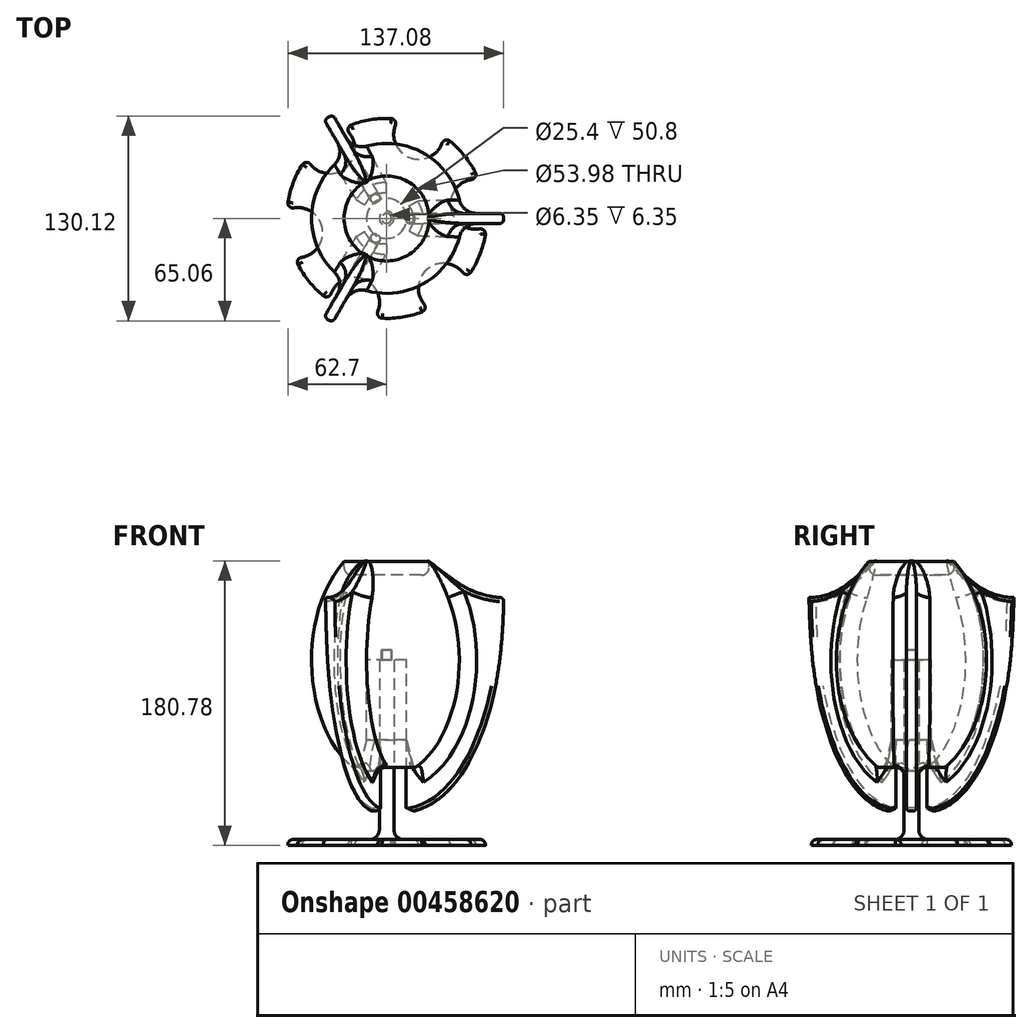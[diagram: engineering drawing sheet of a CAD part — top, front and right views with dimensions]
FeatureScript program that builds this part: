
annotation { "Feature Type Name" : "Feature", "Feature Type Description" : "" }
export const myFeature = defineFeature(function(context is Context, id is Id, definition is map)
    precondition{}
    {
        {
            var Q0;
            Q0=qCreatedBy(makeId("Front.planeOp"),FACE);
            var sketch = newSketch(context, id + "F0", { "sketchPlane" : qUnion([Q0])});
            skEllipticalArc(sketch, "E0", {});
            skLineSegment(sketch, "E1", {"start": v(0, 53.97) * mm, "end": v(0, 6.35) * mm});
            skLineSegment(sketch, "E2", {"start": v(3.18, 0) * mm, "end": v(47.63, 0) * mm});
            skLineSegment(sketch, "E3", {"start": v(12.7, -50.8) * mm, "end": v(35.5, -50.8) * mm});
            skLineSegment(sketch, "E4", {"start": v(0, 53.97) * mm, "end": v(33.62, 53.97) * mm});
            skLineSegment(sketch, "E5", {"start": v(26.99, 53.97) * mm, "end": v(26.99, 62.78) * mm});
            skLineSegment(sketch, "E6", {"start": v(12.7, 0) * mm, "end": v(12.7, -50.8) * mm});
            skLineSegment(sketch, "E7", {"start": v(12.7, -50.8) * mm, "end": v(17.75, -70.71) * mm});
            skPoint(sketch, "E7.endSnap0", {"position": v(17.75, -50.8) * mm});
            skLineSegment(sketch, "E8", {"start": v(3.18, 0) * mm, "end": v(3.17, 6.35) * mm});
            skLineSegment(sketch, "E9", {"start": v(3.17, 6.35) * mm, "end": v(0, 6.35) * mm});
            skPoint(sketch, "E10.orphan", {"position": v(0, -50.8) * mm});
            const initialGuessF0  = {"E0": [0, 0, 0, -1, 0.0762, 0.047625, 0.38189324819891574, 2.539138020204803]};
            skSetInitialGuess(sketch, initialGuessF0);
            skSolve(sketch);
        }
        {
            var Q0;
            Q0=qCreatedBy(makeId("Front.planeOp"),FACE);
            var sketch = newSketch(context, id + "F1", { "sketchPlane" : qUnion([Q0])});
            skSolve(sketch);
        }
        {
            var Q0;
            Q0 = qSketchRegion(id + "F1", true);
            var Q1;
            {var subQ5=sQuery(id+"F0.wireOp",EDGE,"E1");Q1=makeQuery(id+"F0.imprint","IMPRINT",FACE,{"disambiguationData":[TD([[makeQuery(id+"F0.imprint","IMPRINT",EDGE,{"derivedFrom":subQ5}),1.0]])]});}
            var Q2;
            {var subQ3=sQuery(id+"F0.wireOp",EDGE,"E3");Q2=makeQuery(id+"F0.imprint","IMPRINT",FACE,{"disambiguationData":[TD([[makeQuery(id+"F0.imprint","IMPRINT",EDGE,{"derivedFrom":subQ3}),1.0]])]});}
            var Q3;
            {var subQ2=sQuery(id+"F0.wireOp",EDGE,"E3");Q3=makeQuery(id+"F0.imprint","IMPRINT",FACE,{"disambiguationData":[TD([[makeQuery(id+"F0.imprint","IMPRINT",EDGE,{"derivedFrom":subQ2}),-1.0]])]});}
            var Q4;
            {var subQ0=sQuery(id+"F0.wireOp",EDGE,"E5");Q4=makeQuery(id+"F0.imprint","IMPRINT",FACE,{"disambiguationData":[TD([[makeQuery(id+"F0.imprint","IMPRINT",EDGE,{"derivedFrom":subQ0}),-1.0]])]});}
            var Q5;
            Q5=sQuery(id+"F0.wireOp",EDGE,"E1");
            revolve(context, id + "F2", {"entities" : qUnion([Q0, Q1, Q2, Q3, Q4]), "axis" : qUnion([Q5]), "revolveType" : RevolveType.FULL});
        }
        {
            var Q0;
            Q0=qCreatedBy(makeId("Front.planeOp"),FACE);
            var sketch = newSketch(context, id + "F3", { "sketchPlane" : qUnion([Q0])});
            skEllipticalArc(sketch, "E11.0", {});
            skFitSpline(sketch, "E12", {"points": [v(17.75, -96.11) * mm, v(62.2, -43.9) * mm, v(74.95, 39.51) * mm], "startDerivative": vector(138.34, 33.42) * mm, "endDerivative": vector(4.15, 174.83) * mm});
            skFitSpline(sketch, "E13", {"points": [v(26.99, 62.78) * mm, v(52.93, 44.73) * mm, v(74.95, 39.51) * mm], "startDerivative": vector(53.6, -38.1) * mm, "endDerivative": vector(42.04, 0.55) * mm});
            skArc(sketch, "E14", {"start": v(73.77, 14.42) * mm, "mid": v(56.44, 0.7) * mm, "end": v(69.62, -17.04) * mm});
            skFitSpline(sketch, "E15.trimOffspring", {"points": [v(17.75, -96.11) * mm, v(62.2, -43.9) * mm, v(74.95, 39.51) * mm], "startDerivative": vector(138.34, 33.42) * mm, "endDerivative": vector(4.15, 174.83) * mm});
            skEllipticalArc(sketch, "E16.0.2", {});
            skLineSegment(sketch, "E16.0.5", {"start": v(0, 53.97) * mm, "end": v(0, 6.35) * mm});
            skPoint(sketch, "E16.0.0.end.orphan", {"position": v(12.7, 0) * mm});
            skPoint(sketch, "E16.0.3.end.orphan", {"position": v(26.99, 53.97) * mm});
            skPoint(sketch, "E16.0.7.end.orphan", {"position": v(3.18, 0) * mm});
            skPoint(sketch, "E16.0.6.end.orphan", {"position": v(3.17, 6.35) * mm});
            skLineSegment(sketch, "E17.0", {"start": v(12.7, -50.8) * mm, "end": v(17.75, -70.71) * mm});
            skLineSegment(sketch, "E18", {"start": v(17.75, -70.71) * mm, "end": v(12.7, -50.8) * mm});
            skLineSegment(sketch, "E19", {"start": v(12.7, -50.8) * mm, "end": v(12.7, -93.82) * mm});
            skLineSegment(sketch, "E20", {"start": v(17.75, -96.11) * mm, "end": v(12.7, -93.82) * mm});
            const initialGuessF3  = {"E11.0": [0, 0, 0, -1, 0.0762, 0.047625, 0.38189324819891574, 2.579056409045938], "E16.0.2": [0, 0, 0, -1, 0.0762, 0.047625, 1.5707963267948966, 2.300523983021863]};
            skSetInitialGuess(sketch, initialGuessF3);
            skSolve(sketch);
        }
        {
            var Q0;
            Q0 = qSketchRegion(id + "F3", true);
            extrude(context, id + "F4", {"entities" : qUnion([Q0]), "endBound" : BoundingType.SYMMETRIC, "depth" : 6.35 * mm});
        }
        {
            var Q0;
            Q0=makeQuery(id+"F4.opExtrude","SWEPT_BODY",BODY,{"disambiguationData":[OSD([sQuery(id+"F3.wireOp",EDGE,"E11.0"),sQuery(id+"F3.wireOp",EDGE,"7cff1985-20f7-4c6d-82bb-5eb624a96f58"),sQuery(id+"F3.wireOp",EDGE,"E12"),sQuery(id+"F3.wireOp",EDGE,"E13"),sQuery(id+"F3.wireOp",EDGE,"E14"),sQuery(id+"F3.wireOp",EDGE,"E15.trimOffspring"),sQuery(id+"F3.wireOp",EDGE,"E16.0.2")])]});
            var Q1;
            Q1=sQuery(id+"F3.wireOp",EDGE,"E16.0.5");
            circularPattern(context, id + "F5", {"entities" : qUnion([Q0]), "axis" : qUnion([Q1]), "angle" : 360 * degree, "instanceCount" : 3, "equalSpace" : true});
        }
        {
            var Q0;
            Q0=qCreatedBy(makeId("Front.planeOp"),FACE);
            var sketch = newSketch(context, id + "F6", { "sketchPlane" : qUnion([Q0])});
            skPoint(sketch, "E21.0", {"position": v(0, 6.35) * mm});
            skLineSegment(sketch, "E22", {"start": v(0, 6.35) * mm, "end": v(3.05, 6.35) * mm});
            skLineSegment(sketch, "E23", {"start": v(3.05, 6.35) * mm, "end": v(3.05, 0) * mm});
            skLineSegment(sketch, "E24", {"start": v(3.05, 0) * mm, "end": v(4.64, 0) * mm});
            skLineSegment(sketch, "E25", {"start": v(4.64, 0) * mm, "end": v(4.64, -107.58) * mm});
            skLineSegment(sketch, "E26", {"start": v(10.99, -113.93) * mm, "end": v(60.33, -113.93) * mm});
            skLineSegment(sketch, "E27", {"start": v(63.5, -117.1) * mm, "end": v(63.5, -117.74) * mm});
            skLineSegment(sketch, "E28", {"start": v(63.5, -117.74) * mm, "end": v(0, -117.74) * mm});
            skLineSegment(sketch, "E29", {"start": v(0, -117.74) * mm, "end": v(0, 6.35) * mm});
            skPoint(sketch, "E30.visualSharp", {"position": v(4.64, -113.93) * mm});
            skArc(sketch, "E30.filletArc", {"start": v(4.64, -107.58) * mm, "mid": v(6.5, -112.07) * mm, "end": v(10.99, -113.93) * mm});
            skPoint(sketch, "E31.visualSharp", {"position": v(63.5, -113.93) * mm});
            skArc(sketch, "E31.filletArc", {"start": v(63.5, -117.1) * mm, "mid": v(62.57, -114.86) * mm, "end": v(60.33, -113.93) * mm});
            skSolve(sketch);
        }
        {
            var Q0;
            Q0=makeQuery(id+"F6.imprint","IMPRINT",FACE,{"disambiguationData":[TD([[makeQuery(id+"F6.imprint","IMPRINT",EDGE,{"derivedFrom":sQuery(id+"F6.wireOp",EDGE,"E22")}),-1.0]])]});
            var Q1;
            Q1=sQuery(id+"F6.wireOp",EDGE,"E29");
            revolve(context, id + "F7", {"entities" : qUnion([Q0]), "axis" : qUnion([Q1]), "revolveType" : RevolveType.FULL});
        }
        {
            var Q0;
            Q0=makeQuery(id+"F4.opExtrude","CAP_EDGE",EDGE,{"disambiguationData":[OSD([sQuery(id+"F3.wireOp",EDGE,"E13")])],"isStart":false});
            fillet(context, id + "F8", {"entities" : qUnion([Q0]), "radius" : 2.54 * mm, "tangentPropagation" : true, "allowEdgeOverflow" : false});
        }
        {
            var Q0;
            Q0=makeQuery(id+"F4.opExtrude","CAP_EDGE",EDGE,{"disambiguationData":[OSD([sQuery(id+"F3.wireOp",EDGE,"E13")])],"isStart":true});
            var Q1;
            Q1=makeQuery(id+"F4.opExtrude","CAP_EDGE",EDGE,{"disambiguationData":[OSD([sQuery(id+"F3.wireOp",EDGE,"E15.trimOffspring")])],"isStart":false});
            var Q2;
            Q2=makeQuery(id+"F4.opExtrude","CAP_EDGE",EDGE,{"disambiguationData":[OSD([sQuery(id+"F3.wireOp",EDGE,"E15.trimOffspring")])],"isStart":true});
            var Q3;
            Q3=makeQuery(id+"F4.opExtrude","CAP_EDGE",EDGE,{"disambiguationData":[OSD([sQuery(id+"F3.wireOp",EDGE,"E12")])],"isStart":false});
            var Q4;
            Q4=makeQuery(id+"F4.opExtrude","CAP_EDGE",EDGE,{"disambiguationData":[OSD([sQuery(id+"F3.wireOp",EDGE,"E12")])],"isStart":true});
            var Q5;
            Q5=makeQuery(id+"F4.opExtrude","CAP_EDGE",EDGE,{"disambiguationData":[OSD([sQuery(id+"F3.wireOp",EDGE,"E14")])],"isStart":false});
            var Q6;
            Q6=makeQuery(id+"F4.opExtrude","CAP_EDGE",EDGE,{"disambiguationData":[OSD([sQuery(id+"F3.wireOp",EDGE,"E14")])],"isStart":true});
            fillet(context, id + "F9", {"entities" : qUnion([Q0, Q1, Q2, Q3, Q4, Q5, Q6]), "radius" : 2.54 * mm, "tangentPropagation" : true, "allowEdgeOverflow" : false});
        }
        {
            var Q0;
            Q0=makeQuery(id+"F5.opPattern","COPY",EDGE,{"derivedFrom":makeQuery(id+"F4.opExtrude","CAP_EDGE",EDGE,{"disambiguationData":[OSD([sQuery(id+"F3.wireOp",EDGE,"E15.trimOffspring")])],"isStart":false}),"instanceName":"1"});
            var Q1;
            Q1=makeQuery(id+"F5.opPattern","COPY",EDGE,{"derivedFrom":makeQuery(id+"F4.opExtrude","CAP_EDGE",EDGE,{"disambiguationData":[OSD([sQuery(id+"F3.wireOp",EDGE,"E15.trimOffspring")])],"isStart":true}),"instanceName":"1"});
            var Q2;
            Q2=makeQuery(id+"F5.opPattern","COPY",EDGE,{"derivedFrom":makeQuery(id+"F4.opExtrude","CAP_EDGE",EDGE,{"disambiguationData":[OSD([sQuery(id+"F3.wireOp",EDGE,"E14")])],"isStart":false}),"instanceName":"1"});
            var Q3;
            Q3=makeQuery(id+"F5.opPattern","COPY",EDGE,{"derivedFrom":makeQuery(id+"F4.opExtrude","CAP_EDGE",EDGE,{"disambiguationData":[OSD([sQuery(id+"F3.wireOp",EDGE,"E14")])],"isStart":true}),"instanceName":"1"});
            var Q4;
            Q4=makeQuery(id+"F5.opPattern","COPY",EDGE,{"derivedFrom":makeQuery(id+"F4.opExtrude","CAP_EDGE",EDGE,{"disambiguationData":[OSD([sQuery(id+"F3.wireOp",EDGE,"E12")])],"isStart":true}),"instanceName":"1"});
            var Q5;
            Q5=makeQuery(id+"F5.opPattern","COPY",EDGE,{"derivedFrom":makeQuery(id+"F4.opExtrude","CAP_EDGE",EDGE,{"disambiguationData":[OSD([sQuery(id+"F3.wireOp",EDGE,"E12")])],"isStart":false}),"instanceName":"1"});
            var Q6;
            Q6=makeQuery(id+"F5.opPattern","COPY",EDGE,{"derivedFrom":makeQuery(id+"F4.opExtrude","CAP_EDGE",EDGE,{"disambiguationData":[OSD([sQuery(id+"F3.wireOp",EDGE,"E13")])],"isStart":false}),"instanceName":"1"});
            var Q7;
            Q7=makeQuery(id+"F5.opPattern","COPY",EDGE,{"derivedFrom":makeQuery(id+"F4.opExtrude","CAP_EDGE",EDGE,{"disambiguationData":[OSD([sQuery(id+"F3.wireOp",EDGE,"E13")])],"isStart":true}),"instanceName":"1"});
            fillet(context, id + "F10", {"entities" : qUnion([Q0, Q1, Q2, Q3, Q4, Q5, Q6, Q7]), "radius" : 2.54 * mm, "tangentPropagation" : true, "allowEdgeOverflow" : false});
        }
        {
            var Q0;
            Q0=makeQuery(id+"F5.opPattern","COPY",EDGE,{"derivedFrom":makeQuery(id+"F4.opExtrude","CAP_EDGE",EDGE,{"disambiguationData":[OSD([sQuery(id+"F3.wireOp",EDGE,"E12")])],"isStart":true}),"instanceName":"2"});
            var Q1;
            Q1=makeQuery(id+"F5.opPattern","COPY",EDGE,{"derivedFrom":makeQuery(id+"F4.opExtrude","CAP_EDGE",EDGE,{"disambiguationData":[OSD([sQuery(id+"F3.wireOp",EDGE,"E14")])],"isStart":false}),"instanceName":"2"});
            var Q2;
            Q2=makeQuery(id+"F5.opPattern","COPY",EDGE,{"derivedFrom":makeQuery(id+"F4.opExtrude","CAP_EDGE",EDGE,{"disambiguationData":[OSD([sQuery(id+"F3.wireOp",EDGE,"E14")])],"isStart":true}),"instanceName":"2"});
            var Q3;
            Q3=makeQuery(id+"F5.opPattern","COPY",EDGE,{"derivedFrom":makeQuery(id+"F4.opExtrude","CAP_EDGE",EDGE,{"disambiguationData":[OSD([sQuery(id+"F3.wireOp",EDGE,"E15.trimOffspring")])],"isStart":false}),"instanceName":"2"});
            var Q4;
            Q4=makeQuery(id+"F5.opPattern","COPY",EDGE,{"derivedFrom":makeQuery(id+"F4.opExtrude","CAP_EDGE",EDGE,{"disambiguationData":[OSD([sQuery(id+"F3.wireOp",EDGE,"E15.trimOffspring")])],"isStart":true}),"instanceName":"2"});
            var Q5;
            Q5=makeQuery(id+"F5.opPattern","COPY",EDGE,{"derivedFrom":makeQuery(id+"F4.opExtrude","CAP_EDGE",EDGE,{"disambiguationData":[OSD([sQuery(id+"F3.wireOp",EDGE,"E13")])],"isStart":false}),"instanceName":"2"});
            var Q6;
            Q6=makeQuery(id+"F5.opPattern","COPY",EDGE,{"derivedFrom":makeQuery(id+"F4.opExtrude","CAP_EDGE",EDGE,{"disambiguationData":[OSD([sQuery(id+"F3.wireOp",EDGE,"E13")])],"isStart":true}),"instanceName":"2"});
            var Q7;
            Q7=makeQuery(id+"F5.opPattern","COPY",EDGE,{"derivedFrom":makeQuery(id+"F4.opExtrude","CAP_EDGE",EDGE,{"disambiguationData":[OSD([sQuery(id+"F3.wireOp",EDGE,"E12")])],"isStart":false}),"instanceName":"2"});
            fillet(context, id + "F11", {"entities" : qUnion([Q0, Q1, Q2, Q3, Q4, Q5, Q6, Q7]), "radius" : 2.54 * mm, "tangentPropagation" : true, "allowEdgeOverflow" : false});
        }
        {
            var Q0;
            Q0=makeQuery(id+"F5.opPattern","COPY",EDGE,{"derivedFrom":makeQuery(id+"F4.opExtrude","CAP_EDGE",EDGE,{"disambiguationData":[OSD([sQuery(id+"F3.wireOp",EDGE,"E19")])],"isStart":false}),"instanceName":"1"});
            var Q1;
            Q1=makeQuery(id+"F5.opPattern","COPY",EDGE,{"derivedFrom":makeQuery(id+"F4.opExtrude","CAP_EDGE",EDGE,{"disambiguationData":[OSD([sQuery(id+"F3.wireOp",EDGE,"E19")])],"isStart":true}),"instanceName":"1"});
            var Q2;
            Q2=makeQuery(id+"F10.opFillet","BLEND_EDGE",EDGE,{"blendedFrom":[makeQuery(id+"F5.opPattern","COPY",EDGE,{"derivedFrom":makeQuery(id+"F4.opExtrude","CAP_EDGE",EDGE,{"disambiguationData":[OSD([sQuery(id+"F3.wireOp",EDGE,"E12")])],"isStart":false}),"instanceName":"1"}),makeQuery(id+"F5.opPattern","COPY",FACE,{"derivedFrom":makeQuery(id+"F4.opExtrude","SWEPT_FACE",FACE,{"disambiguationData":[OSD([sQuery(id+"F3.wireOp",EDGE,"E20")])]}),"instanceName":"1"})],"blendedInto":[makeQuery(id+"F5.opPattern","COPY",FACE,{"derivedFrom":makeQuery(id+"F4.opExtrude","SWEPT_FACE",FACE,{"disambiguationData":[OSD([sQuery(id+"F3.wireOp",EDGE,"E20")])]}),"instanceName":"1"})]});
            var Q3;
            Q3=makeQuery(id+"F10.opFillet","BLEND_EDGE",EDGE,{"blendedFrom":[makeQuery(id+"F5.opPattern","COPY",EDGE,{"derivedFrom":makeQuery(id+"F4.opExtrude","CAP_EDGE",EDGE,{"disambiguationData":[OSD([sQuery(id+"F3.wireOp",EDGE,"E12")])],"isStart":true}),"instanceName":"1"}),makeQuery(id+"F5.opPattern","COPY",FACE,{"derivedFrom":makeQuery(id+"F4.opExtrude","SWEPT_FACE",FACE,{"disambiguationData":[OSD([sQuery(id+"F3.wireOp",EDGE,"E20")])]}),"instanceName":"1"})],"blendedInto":[makeQuery(id+"F5.opPattern","COPY",FACE,{"derivedFrom":makeQuery(id+"F4.opExtrude","SWEPT_FACE",FACE,{"disambiguationData":[OSD([sQuery(id+"F3.wireOp",EDGE,"E20")])]}),"instanceName":"1"})]});
            var Q4;
            Q4=makeQuery(id+"F4.opExtrude","CAP_EDGE",EDGE,{"disambiguationData":[OSD([sQuery(id+"F3.wireOp",EDGE,"E19")])],"isStart":false});
            var Q5;
            Q5=makeQuery(id+"F4.opExtrude","CAP_EDGE",EDGE,{"disambiguationData":[OSD([sQuery(id+"F3.wireOp",EDGE,"E19")])],"isStart":true});
            var Q6;
            Q6=makeQuery(id+"F9.opFillet","BLEND_EDGE",EDGE,{"blendedFrom":[makeQuery(id+"F4.opExtrude","CAP_EDGE",EDGE,{"disambiguationData":[OSD([sQuery(id+"F3.wireOp",EDGE,"E12")])],"isStart":false}),makeQuery(id+"F4.opExtrude","SWEPT_FACE",FACE,{"disambiguationData":[OSD([sQuery(id+"F3.wireOp",EDGE,"E20")])]})],"blendedInto":[makeQuery(id+"F4.opExtrude","SWEPT_FACE",FACE,{"disambiguationData":[OSD([sQuery(id+"F3.wireOp",EDGE,"E20")])]})]});
            var Q7;
            Q7=makeQuery(id+"F5.opPattern","COPY",EDGE,{"derivedFrom":makeQuery(id+"F4.opExtrude","CAP_EDGE",EDGE,{"disambiguationData":[OSD([sQuery(id+"F3.wireOp",EDGE,"E19")])],"isStart":true}),"instanceName":"2"});
            var Q8;
            Q8=makeQuery(id+"F5.opPattern","COPY",EDGE,{"derivedFrom":makeQuery(id+"F4.opExtrude","CAP_EDGE",EDGE,{"disambiguationData":[OSD([sQuery(id+"F3.wireOp",EDGE,"E19")])],"isStart":false}),"instanceName":"2"});
            var Q9;
            Q9=makeQuery(id+"F11.opFillet","BLEND_EDGE",EDGE,{"blendedFrom":[makeQuery(id+"F5.opPattern","COPY",EDGE,{"derivedFrom":makeQuery(id+"F4.opExtrude","CAP_EDGE",EDGE,{"disambiguationData":[OSD([sQuery(id+"F3.wireOp",EDGE,"E12")])],"isStart":true}),"instanceName":"2"}),makeQuery(id+"F5.opPattern","COPY",FACE,{"derivedFrom":makeQuery(id+"F4.opExtrude","SWEPT_FACE",FACE,{"disambiguationData":[OSD([sQuery(id+"F3.wireOp",EDGE,"E20")])]}),"instanceName":"2"})],"blendedInto":[makeQuery(id+"F5.opPattern","COPY",FACE,{"derivedFrom":makeQuery(id+"F4.opExtrude","SWEPT_FACE",FACE,{"disambiguationData":[OSD([sQuery(id+"F3.wireOp",EDGE,"E20")])]}),"instanceName":"2"})]});
            fillet(context, id + "F12", {"entities" : qUnion([Q0, Q1, Q2, Q3, Q4, Q5, Q6, Q7, Q8, Q9]), "radius" : 2.54 * mm, "tangentPropagation" : true, "allowEdgeOverflow" : false});
        }
        {
            var Q0;
            Q0=makeQuery(id+"F2.opRevolve","SWEPT_EDGE",EDGE,{"disambiguationData":[OSD([sQuery(id+"F0.wireOp",EDGE,"E4"),sQuery(id+"F0.wireOp",EDGE,"E5")])]});
            fillet(context, id + "F13", {"entities" : qUnion([Q0]), "radius" : 5.08 * mm, "tangentPropagation" : true, "allowEdgeOverflow" : false});
        }
        {
            var Q0;
            Q0=makeQuery(id+"F5.opPattern","COPY",BODY,{"derivedFrom":makeQuery(id+"F4.opExtrude","SWEPT_BODY",BODY,{"disambiguationData":[OSD([sQuery(id+"F3.wireOp",EDGE,"E11.0"),sQuery(id+"F3.wireOp",EDGE,"E12"),sQuery(id+"F3.wireOp",EDGE,"E13"),sQuery(id+"F3.wireOp",EDGE,"E14"),sQuery(id+"F3.wireOp",EDGE,"E15.trimOffspring"),sQuery(id+"F3.wireOp",EDGE,"E16.0.2"),sQuery(id+"F3.wireOp",EDGE,"E18"),sQuery(id+"F3.wireOp",EDGE,"E19"),sQuery(id+"F3.wireOp",EDGE,"E20")])]}),"instanceName":"2"});
            transform(context, id + "F14", {"entities" : qUnion([Q0]), "transformType" : TransformType.TRANSLATION_3D, "dx" : 0.5 * mm, "dy" : -0.5 * mm, "dz" : 0.25 * mm, "makeCopy" : false});
        }
        {
            var Q0;
            Q0=makeQuery(id+"F5.opPattern","COPY",BODY,{"derivedFrom":makeQuery(id+"F4.opExtrude","SWEPT_BODY",BODY,{"disambiguationData":[OSD([sQuery(id+"F3.wireOp",EDGE,"E11.0"),sQuery(id+"F3.wireOp",EDGE,"E12"),sQuery(id+"F3.wireOp",EDGE,"E13"),sQuery(id+"F3.wireOp",EDGE,"E14"),sQuery(id+"F3.wireOp",EDGE,"E15.trimOffspring"),sQuery(id+"F3.wireOp",EDGE,"E16.0.2"),sQuery(id+"F3.wireOp",EDGE,"E18"),sQuery(id+"F3.wireOp",EDGE,"E19"),sQuery(id+"F3.wireOp",EDGE,"E20")])]}),"instanceName":"1"});
            transform(context, id + "F15", {"entities" : qUnion([Q0]), "transformType" : TransformType.TRANSLATION_3D, "dx" : 0.5 * mm, "dy" : 0.5 * mm, "dz" : 0.25 * mm, "makeCopy" : false});
        }
        {
            var Q0;
            Q0=makeQuery(id+"F4.opExtrude","SWEPT_BODY",BODY,{"disambiguationData":[OSD([sQuery(id+"F3.wireOp",EDGE,"E11.0"),sQuery(id+"F3.wireOp",EDGE,"E12"),sQuery(id+"F3.wireOp",EDGE,"E13"),sQuery(id+"F3.wireOp",EDGE,"E14"),sQuery(id+"F3.wireOp",EDGE,"E15.trimOffspring"),sQuery(id+"F3.wireOp",EDGE,"E16.0.2"),sQuery(id+"F3.wireOp",EDGE,"E18"),sQuery(id+"F3.wireOp",EDGE,"E19"),sQuery(id+"F3.wireOp",EDGE,"E20")])]});
            transform(context, id + "F16", {"entities" : qUnion([Q0]), "transformType" : TransformType.TRANSLATION_3D, "dx" : -0.5 * mm, "dy" : 0 * mm, "dz" : 0.25 * mm, "makeCopy" : false});
        }
        {
            var Q0;
            Q0=makeQuery(id+"F2.opRevolve","SWEPT_BODY",BODY,{"disambiguationData":[OSD([sQuery(id+"F0.wireOp",EDGE,"E0"),sQuery(id+"F0.wireOp",EDGE,"E1"),sQuery(id+"F0.wireOp",EDGE,"E2"),sQuery(id+"F0.wireOp",EDGE,"E4"),sQuery(id+"F0.wireOp",EDGE,"E5"),sQuery(id+"F0.wireOp",EDGE,"E6"),sQuery(id+"F0.wireOp",EDGE,"E7"),sQuery(id+"F0.wireOp",EDGE,"E8"),sQuery(id+"F0.wireOp",EDGE,"E9")])]});
            var Q1;
            Q1=makeQuery(id+"F4.opExtrude","SWEPT_BODY",BODY,{"disambiguationData":[OSD([sQuery(id+"F3.wireOp",EDGE,"E11.0"),sQuery(id+"F3.wireOp",EDGE,"E12"),sQuery(id+"F3.wireOp",EDGE,"E13"),sQuery(id+"F3.wireOp",EDGE,"E14"),sQuery(id+"F3.wireOp",EDGE,"E15.trimOffspring"),sQuery(id+"F3.wireOp",EDGE,"E16.0.2"),sQuery(id+"F3.wireOp",EDGE,"E18"),sQuery(id+"F3.wireOp",EDGE,"E19"),sQuery(id+"F3.wireOp",EDGE,"E20")])]});
            var Q2;
            Q2=makeQuery(id+"F5.opPattern","COPY",BODY,{"derivedFrom":makeQuery(id+"F4.opExtrude","SWEPT_BODY",BODY,{"disambiguationData":[OSD([sQuery(id+"F3.wireOp",EDGE,"E11.0"),sQuery(id+"F3.wireOp",EDGE,"E12"),sQuery(id+"F3.wireOp",EDGE,"E13"),sQuery(id+"F3.wireOp",EDGE,"E14"),sQuery(id+"F3.wireOp",EDGE,"E15.trimOffspring"),sQuery(id+"F3.wireOp",EDGE,"E16.0.2"),sQuery(id+"F3.wireOp",EDGE,"E18"),sQuery(id+"F3.wireOp",EDGE,"E19"),sQuery(id+"F3.wireOp",EDGE,"E20")])]}),"instanceName":"1"});
            var Q3;
            Q3=makeQuery(id+"F5.opPattern","COPY",BODY,{"derivedFrom":makeQuery(id+"F4.opExtrude","SWEPT_BODY",BODY,{"disambiguationData":[OSD([sQuery(id+"F3.wireOp",EDGE,"E11.0"),sQuery(id+"F3.wireOp",EDGE,"E12"),sQuery(id+"F3.wireOp",EDGE,"E13"),sQuery(id+"F3.wireOp",EDGE,"E14"),sQuery(id+"F3.wireOp",EDGE,"E15.trimOffspring"),sQuery(id+"F3.wireOp",EDGE,"E16.0.2"),sQuery(id+"F3.wireOp",EDGE,"E18"),sQuery(id+"F3.wireOp",EDGE,"E19"),sQuery(id+"F3.wireOp",EDGE,"E20")])]}),"instanceName":"2"});
            booleanBodies(context, id + "F17", {"operationType" : BooleanOperationType.UNION, "tools" : qUnion([Q0, Q1, Q2, Q3])});
        }
        {
            var Q0;
            Q0=makeQuery(id+"F17.opBoolean","INTERSECT",EDGE,{"derivedFrom":[makeQuery(id+"F2.opRevolve","SWEPT_FACE",FACE,{"disambiguationData":[OSD([sQuery(id+"F0.wireOp",EDGE,"E0")])]}),makeQuery(id+"F4.opExtrude","CAP_FACE",FACE,{"disambiguationData":[OSD([sQuery(id+"F3.wireOp",EDGE,"E11.0"),sQuery(id+"F3.wireOp",EDGE,"E12"),sQuery(id+"F3.wireOp",EDGE,"E13"),sQuery(id+"F3.wireOp",EDGE,"E14"),sQuery(id+"F3.wireOp",EDGE,"E15.trimOffspring"),sQuery(id+"F3.wireOp",EDGE,"E16.0.2"),sQuery(id+"F3.wireOp",EDGE,"E18"),sQuery(id+"F3.wireOp",EDGE,"E19"),sQuery(id+"F3.wireOp",EDGE,"E20")])],"isStart":false})]});
            var Q1;
            Q1=makeQuery(id+"F17.opBoolean","INTERSECT",EDGE,{"derivedFrom":[makeQuery(id+"F2.opRevolve","SWEPT_FACE",FACE,{"disambiguationData":[OSD([sQuery(id+"F0.wireOp",EDGE,"E0")])]}),makeQuery(id+"F5.opPattern","COPY",FACE,{"derivedFrom":makeQuery(id+"F4.opExtrude","CAP_FACE",FACE,{"disambiguationData":[OSD([sQuery(id+"F3.wireOp",EDGE,"E11.0"),sQuery(id+"F3.wireOp",EDGE,"E12"),sQuery(id+"F3.wireOp",EDGE,"E13"),sQuery(id+"F3.wireOp",EDGE,"E14"),sQuery(id+"F3.wireOp",EDGE,"E15.trimOffspring"),sQuery(id+"F3.wireOp",EDGE,"E16.0.2"),sQuery(id+"F3.wireOp",EDGE,"E18"),sQuery(id+"F3.wireOp",EDGE,"E19"),sQuery(id+"F3.wireOp",EDGE,"E20")])],"isStart":true}),"instanceName":"1"})]});
            var Q2;
            Q2=makeQuery(id+"F17.opBoolean","INTERSECT",EDGE,{"derivedFrom":[makeQuery(id+"F2.opRevolve","SWEPT_FACE",FACE,{"disambiguationData":[OSD([sQuery(id+"F0.wireOp",EDGE,"E0")])]}),makeQuery(id+"F5.opPattern","COPY",FACE,{"derivedFrom":makeQuery(id+"F4.opExtrude","CAP_FACE",FACE,{"disambiguationData":[OSD([sQuery(id+"F3.wireOp",EDGE,"E11.0"),sQuery(id+"F3.wireOp",EDGE,"E12"),sQuery(id+"F3.wireOp",EDGE,"E13"),sQuery(id+"F3.wireOp",EDGE,"E14"),sQuery(id+"F3.wireOp",EDGE,"E15.trimOffspring"),sQuery(id+"F3.wireOp",EDGE,"E16.0.2"),sQuery(id+"F3.wireOp",EDGE,"E18"),sQuery(id+"F3.wireOp",EDGE,"E19"),sQuery(id+"F3.wireOp",EDGE,"E20")])],"isStart":true}),"instanceName":"2"})]});
            fillet(context, id + "F18", {"entities" : qUnion([Q0, Q1, Q2]), "radius" : 11.43 * mm, "tangentPropagation" : true, "allowEdgeOverflow" : false});
        }
        {
            var Q0;
            {var subQ0=sQuery(id+"F0.wireOp",EDGE,"E0");var subQ1=sQuery(id+"F0.wireOp",EDGE,"E7");var subQ2=sQuery(id+"F3.wireOp",EDGE,"E20");var subQ3=sQuery(id+"F3.wireOp",EDGE,"E19");var subQ4=sQuery(id+"F3.wireOp",EDGE,"E18");var subQ5=sQuery(id+"F3.wireOp",EDGE,"E16.0.2");var subQ6=sQuery(id+"F3.wireOp",EDGE,"E15.trimOffspring");var subQ7=sQuery(id+"F3.wireOp",EDGE,"E14");var subQ8=sQuery(id+"F3.wireOp",EDGE,"E13");var subQ9=sQuery(id+"F3.wireOp",EDGE,"E12");var subQ10=sQuery(id+"F3.wireOp",EDGE,"E11.0");Q0=makeQuery(id+"F17.opBoolean","SPLIT",EDGE,{"disambiguationData":[TD([makeQuery(id+"F4.opExtrude","CAP_FACE",FACE,{"disambiguationData":[OSD([subQ10,subQ9,subQ8,subQ7,subQ6,subQ5,subQ4,subQ3,subQ2])],"isStart":true})])],"derivedFrom":makeQuery(id+"F2.opRevolve","SWEPT_EDGE",EDGE,{"disambiguationData":[OSD([subQ0,subQ1])]})});}
            var Q1;
            {var subQ0=sQuery(id+"F0.wireOp",EDGE,"E0");var subQ1=sQuery(id+"F0.wireOp",EDGE,"E7");var subQ2=sQuery(id+"F3.wireOp",EDGE,"E20");var subQ3=sQuery(id+"F3.wireOp",EDGE,"E19");var subQ4=sQuery(id+"F3.wireOp",EDGE,"E18");var subQ5=sQuery(id+"F3.wireOp",EDGE,"E16.0.2");var subQ6=sQuery(id+"F3.wireOp",EDGE,"E15.trimOffspring");var subQ7=sQuery(id+"F3.wireOp",EDGE,"E14");var subQ8=sQuery(id+"F3.wireOp",EDGE,"E13");var subQ9=sQuery(id+"F3.wireOp",EDGE,"E12");var subQ10=sQuery(id+"F3.wireOp",EDGE,"E11.0");Q1=makeQuery(id+"F17.opBoolean","SPLIT",EDGE,{"disambiguationData":[TD([makeQuery(id+"F5.opPattern","COPY",FACE,{"derivedFrom":makeQuery(id+"F4.opExtrude","CAP_FACE",FACE,{"disambiguationData":[OSD([subQ10,subQ9,subQ8,subQ7,subQ6,subQ5,subQ4,subQ3,subQ2])],"isStart":false}),"instanceName":"1"})])],"derivedFrom":makeQuery(id+"F2.opRevolve","SWEPT_EDGE",EDGE,{"disambiguationData":[OSD([subQ0,subQ1])]})});}
            var Q2;
            {var subQ0=sQuery(id+"F0.wireOp",EDGE,"E0");var subQ1=sQuery(id+"F0.wireOp",EDGE,"E7");var subQ2=sQuery(id+"F3.wireOp",EDGE,"E20");var subQ3=sQuery(id+"F3.wireOp",EDGE,"E19");var subQ4=sQuery(id+"F3.wireOp",EDGE,"E18");var subQ5=sQuery(id+"F3.wireOp",EDGE,"E16.0.2");var subQ6=sQuery(id+"F3.wireOp",EDGE,"E15.trimOffspring");var subQ7=sQuery(id+"F3.wireOp",EDGE,"E14");var subQ8=sQuery(id+"F3.wireOp",EDGE,"E13");var subQ9=sQuery(id+"F3.wireOp",EDGE,"E12");var subQ10=sQuery(id+"F3.wireOp",EDGE,"E11.0");Q2=makeQuery(id+"F17.opBoolean","SPLIT",EDGE,{"disambiguationData":[TD([makeQuery(id+"F4.opExtrude","CAP_FACE",FACE,{"disambiguationData":[OSD([subQ10,subQ9,subQ8,subQ7,subQ6,subQ5,subQ4,subQ3,subQ2])],"isStart":false})])],"derivedFrom":makeQuery(id+"F2.opRevolve","SWEPT_EDGE",EDGE,{"disambiguationData":[OSD([subQ0,subQ1])]})});}
            fillet(context, id + "F19", {"entities" : qUnion([Q0, Q1, Q2]), "radius" : 3.8 * mm, "tangentPropagation" : true, "allowEdgeOverflow" : false});
        }
        {
            var Q0;
            Q0=makeQuery(id+"F7.opRevolve","SWEPT_FACE",FACE,{"disambiguationData":[OSD([sQuery(id+"F6.wireOp",EDGE,"E28")])]});
            var sketch = newSketch(context, id + "F20", { "sketchPlane" : qUnion([Q0])});
            skCircle(sketch, "E32", {"center": v(-20.4, 53.39) * mm, "radius": 15.88 * mm});
            skPoint(sketch, "E33.0", {"position": v(0, 0) * mm});
            skSolve(sketch);
        }
        {
            var Q0;
            Q0 = qSketchRegion(id + "F20", true);
            extrude(context, id + "F21", {"entities" : qUnion([Q0]), "endBound" : BoundingType.SYMMETRIC, "oppositeDirection" : true, "depth" : 12.7 * mm});
        }
        {
            var Q0;
            Q0=makeQuery(id+"F21.opExtrude","SWEPT_BODY",BODY,{"disambiguationData":[OSD([sQuery(id+"F20.wireOp",EDGE,"E32")])]});
            var Q1;
            Q1=sQuery(id+"F6.wireOp",EDGE,"E29");
            circularPattern(context, id + "F22", {"entities" : qUnion([Q0]), "axis" : qUnion([Q1]), "angle" : 360 * degree, "instanceCount" : 6, "equalSpace" : true});
        }
        {
            var Q0;
            Q0=makeQuery(id+"F22.opPattern","COPY",BODY,{"derivedFrom":makeQuery(id+"F21.opExtrude","SWEPT_BODY",BODY,{"disambiguationData":[OSD([sQuery(id+"F20.wireOp",EDGE,"E32")])]}),"instanceName":"3"});
            var Q1;
            Q1=makeQuery(id+"F22.opPattern","COPY",BODY,{"derivedFrom":makeQuery(id+"F21.opExtrude","SWEPT_BODY",BODY,{"disambiguationData":[OSD([sQuery(id+"F20.wireOp",EDGE,"E32")])]}),"instanceName":"4"});
            var Q2;
            Q2=makeQuery(id+"F21.opExtrude","SWEPT_BODY",BODY,{"disambiguationData":[OSD([sQuery(id+"F20.wireOp",EDGE,"E32")])]});
            var Q3;
            Q3=makeQuery(id+"F22.opPattern","COPY",BODY,{"derivedFrom":makeQuery(id+"F21.opExtrude","SWEPT_BODY",BODY,{"disambiguationData":[OSD([sQuery(id+"F20.wireOp",EDGE,"E32")])]}),"instanceName":"1"});
            var Q4;
            Q4=makeQuery(id+"F22.opPattern","COPY",BODY,{"derivedFrom":makeQuery(id+"F21.opExtrude","SWEPT_BODY",BODY,{"disambiguationData":[OSD([sQuery(id+"F20.wireOp",EDGE,"E32")])]}),"instanceName":"2"});
            var Q5;
            Q5=makeQuery(id+"F22.opPattern","COPY",BODY,{"derivedFrom":makeQuery(id+"F21.opExtrude","SWEPT_BODY",BODY,{"disambiguationData":[OSD([sQuery(id+"F20.wireOp",EDGE,"E32")])]}),"instanceName":"5"});
            var Q6;
            Q6=makeQuery(id+"F7.opRevolve","SWEPT_BODY",BODY,{"disambiguationData":[OSD([sQuery(id+"F6.wireOp",EDGE,"E22"),sQuery(id+"F6.wireOp",EDGE,"E23"),sQuery(id+"F6.wireOp",EDGE,"E24"),sQuery(id+"F6.wireOp",EDGE,"E25"),sQuery(id+"F6.wireOp",EDGE,"E26"),sQuery(id+"F6.wireOp",EDGE,"E27"),sQuery(id+"F6.wireOp",EDGE,"E28"),sQuery(id+"F6.wireOp",EDGE,"E29"),sQuery(id+"F6.wireOp",EDGE,"E30.filletArc"),sQuery(id+"F6.wireOp",EDGE,"E31.filletArc")])]});
            booleanBodies(context, id + "F23", {"operationType" : BooleanOperationType.SUBTRACTION, "tools" : qUnion([Q0, Q1, Q2, Q3, Q4, Q5]), "targets" : qUnion([Q6])});
        }
        {
            var Q0;
            Q0=makeQuery(id+"F23.opBoolean","INTERSECT",EDGE,{"derivedFrom":[makeQuery(id+"F7.opRevolve","SWEPT_FACE",FACE,{"disambiguationData":[OSD([sQuery(id+"F6.wireOp",EDGE,"E26")])]}),makeQuery(id+"F22.opPattern","COPY",FACE,{"derivedFrom":makeQuery(id+"F21.opExtrude","SWEPT_FACE",FACE,{"disambiguationData":[OSD([sQuery(id+"F20.wireOp",EDGE,"E32")])]}),"instanceName":"4"})]});
            var Q1;
            Q1=makeQuery(id+"F23.opBoolean","INTERSECT",EDGE,{"derivedFrom":[makeQuery(id+"F7.opRevolve","SWEPT_FACE",FACE,{"disambiguationData":[OSD([sQuery(id+"F6.wireOp",EDGE,"E26")])]}),makeQuery(id+"F22.opPattern","COPY",FACE,{"derivedFrom":makeQuery(id+"F21.opExtrude","SWEPT_FACE",FACE,{"disambiguationData":[OSD([sQuery(id+"F20.wireOp",EDGE,"E32")])]}),"instanceName":"3"})]});
            var Q2;
            Q2=makeQuery(id+"F23.opBoolean","INTERSECT",EDGE,{"derivedFrom":[makeQuery(id+"F7.opRevolve","SWEPT_FACE",FACE,{"disambiguationData":[OSD([sQuery(id+"F6.wireOp",EDGE,"E26")])]}),makeQuery(id+"F22.opPattern","COPY",FACE,{"derivedFrom":makeQuery(id+"F21.opExtrude","SWEPT_FACE",FACE,{"disambiguationData":[OSD([sQuery(id+"F20.wireOp",EDGE,"E32")])]}),"instanceName":"2"})]});
            var Q3;
            Q3=makeQuery(id+"F23.opBoolean","INTERSECT",EDGE,{"derivedFrom":[makeQuery(id+"F7.opRevolve","SWEPT_FACE",FACE,{"disambiguationData":[OSD([sQuery(id+"F6.wireOp",EDGE,"E26")])]}),makeQuery(id+"F22.opPattern","COPY",FACE,{"derivedFrom":makeQuery(id+"F21.opExtrude","SWEPT_FACE",FACE,{"disambiguationData":[OSD([sQuery(id+"F20.wireOp",EDGE,"E32")])]}),"instanceName":"1"})]});
            var Q4;
            Q4=makeQuery(id+"F23.opBoolean","INTERSECT",EDGE,{"derivedFrom":[makeQuery(id+"F7.opRevolve","SWEPT_FACE",FACE,{"disambiguationData":[OSD([sQuery(id+"F6.wireOp",EDGE,"E26")])]}),makeQuery(id+"F21.opExtrude","SWEPT_FACE",FACE,{"disambiguationData":[OSD([sQuery(id+"F20.wireOp",EDGE,"E32")])]})]});
            var Q5;
            Q5=makeQuery(id+"F23.opBoolean","INTERSECT",EDGE,{"derivedFrom":[makeQuery(id+"F7.opRevolve","SWEPT_FACE",FACE,{"disambiguationData":[OSD([sQuery(id+"F6.wireOp",EDGE,"E26")])]}),makeQuery(id+"F22.opPattern","COPY",FACE,{"derivedFrom":makeQuery(id+"F21.opExtrude","SWEPT_FACE",FACE,{"disambiguationData":[OSD([sQuery(id+"F20.wireOp",EDGE,"E32")])]}),"instanceName":"5"})]});
            fillet(context, id + "F24", {"entities" : qUnion([Q0, Q1, Q2, Q3, Q4, Q5]), "radius" : 3.17 * mm, "tangentPropagation" : true, "allowEdgeOverflow" : false});
        }
    });
